# Revit family: Plumbing_Joints_Aignep_Condense-Drain-90986
name_source: partatom
category: Pipe Accessories
revit_build: Autodesk Revit 2018 (Build: 20170223_1515(x64)
units: mm (PartAtom-declared; Revit-internal decimal feet)

## family parameters
Always vertical = Yes
Cut with Voids When Loaded = No
OmniClass Number = 23.27.43.00
Part Type = Normal
Round Connector Dimension = Use Diameter
Shared = No
Work Plane-Based = No

## types (2) — shared parameters
Assembly Code = D2040100
BIMobject category = Joints
Description = Condense drain
Design country = Italy
Edition number = 1
IFC Classification = Pipe Fitting
Keynote = 15410
Manufacturer = Aignep Spa
Manufacturer country = Italy
Manufacturer name = Aignep Spa
Material main = Plastic
Model = 90986
OmniClass Code = 23-27 43 00
OmniClass Description = Pipe Fittings
Product Guid = b16c0e61-c1b7-4f6b-93f3-74b1300954bf
Product Material = AIGNEP - Aluminium - Grey
Product SKU = Condense-Drain-90986
Product certification = https://www.aignep.com
Product data url = https://www.bimobject.com
Product family = INFINITY
Product group = Fittings
Product name = Condense Drain - 90986
Product url = https://www.aignep.com
QR code = https://www.bimobject.com
URL = https://www.aignep.com

## type names (no varying parameters)
- F 1/2" - Manual
- F 1/2" - Automatic

## geometry (parser evidence)
native form markers: Sweep x2
no freeform markers — native parametric forms only
